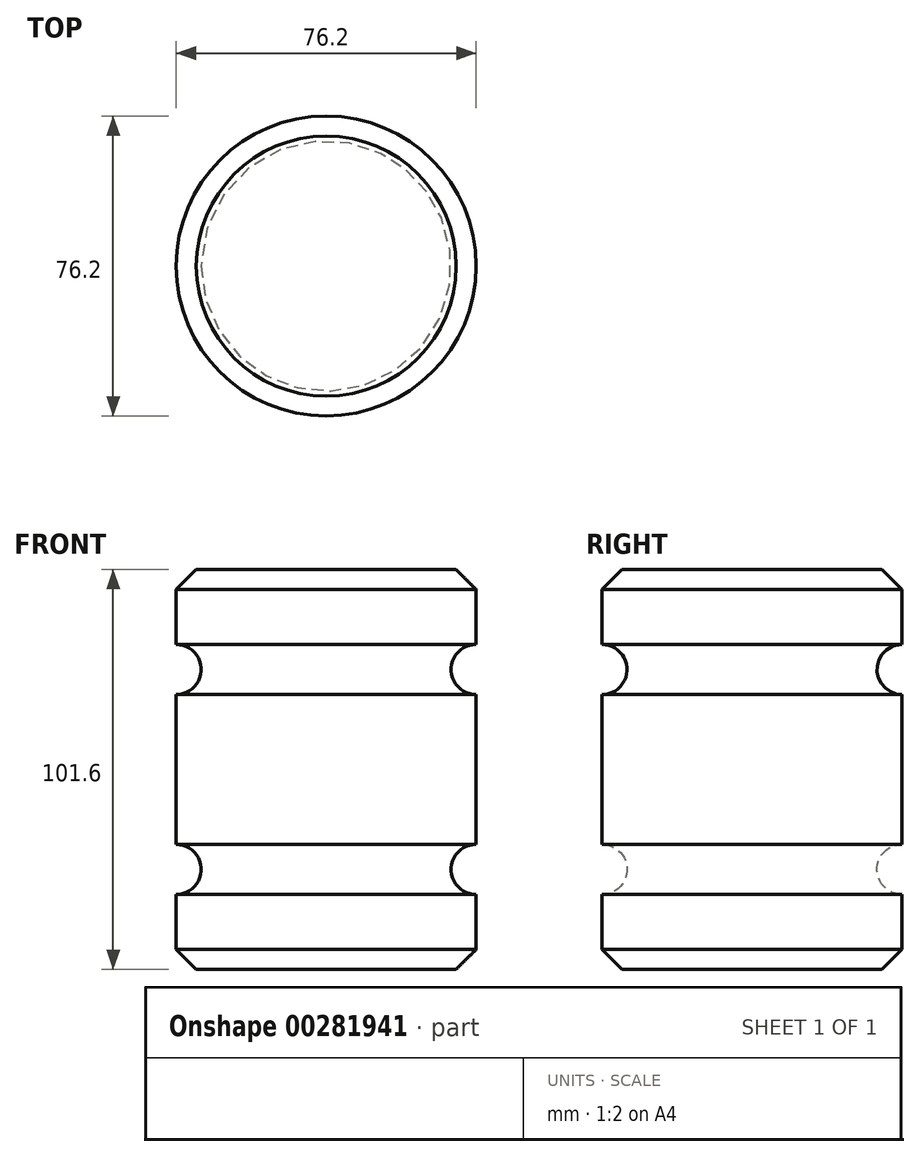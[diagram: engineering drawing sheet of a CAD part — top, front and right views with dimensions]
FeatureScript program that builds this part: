
annotation { "Feature Type Name" : "Feature", "Feature Type Description" : "" }
export const myFeature = defineFeature(function(context is Context, id is Id, definition is map)
    precondition{}
    {
        {
            var Q0;
            Q0=qCreatedBy(makeId("Front.planeOp"),FACE);
            var sketch = newSketch(context, id + "F0", { "sketchPlane" : qUnion([Q0])});
            skLineSegment(sketch, "E0.bottom", {"start": v(0, 0) * mm, "end": v(-38.1, 0) * mm});
            skLineSegment(sketch, "E0.top", {"start": v(0, 101.6) * mm, "end": v(-38.1, 101.6) * mm});
            skLineSegment(sketch, "E0.left", {"start": v(0, 0) * mm, "end": v(0, 19.05) * mm});
            skLineSegment(sketch, "E0.right", {"start": v(-38.1, 0) * mm, "end": v(-38.1, 101.6) * mm});
            skArc(sketch, "E1", {"start": v(0, 82.55) * mm, "mid": v(-6.35, 76.2) * mm, "end": v(0, 69.85) * mm});
            skArc(sketch, "E2", {"start": v(0, 31.75) * mm, "mid": v(-6.35, 25.4) * mm, "end": v(0, 19.05) * mm});
            skLineSegment(sketch, "E3.trimOffspring", {"start": v(0, 82.55) * mm, "end": v(0, 101.6) * mm});
            skLineSegment(sketch, "E4.trimOffspring", {"start": v(0, 31.75) * mm, "end": v(0, 69.85) * mm});
            skSolve(sketch);
        }
        {
            var Q0;
            Q0 = qSketchRegion(id + "F0", true);
            var Q1;
            Q1=sQuery(id+"F0.wireOp",EDGE,"E0.right");
            revolve(context, id + "F1", {"entities" : qUnion([Q0]), "axis" : qUnion([Q1]), "revolveType" : RevolveType.FULL});
        }
        {
            var Q0;
            Q0=makeQuery(id+"F1.opRevolve","SWEPT_FACE",FACE,{"disambiguationData":[OSD([sQuery(id+"F0.wireOp",EDGE,"E0.top")])]});
            var Q1;
            Q1=makeQuery(id+"F1.opRevolve","SWEPT_FACE",FACE,{"disambiguationData":[OSD([sQuery(id+"F0.wireOp",EDGE,"E0.bottom")])]});
            chamfer(context, id + "F2", {"entities" : qUnion([Q0, Q1]), "width" : 5.08 * mm, "tangentPropagation" : true});
        }
    });
